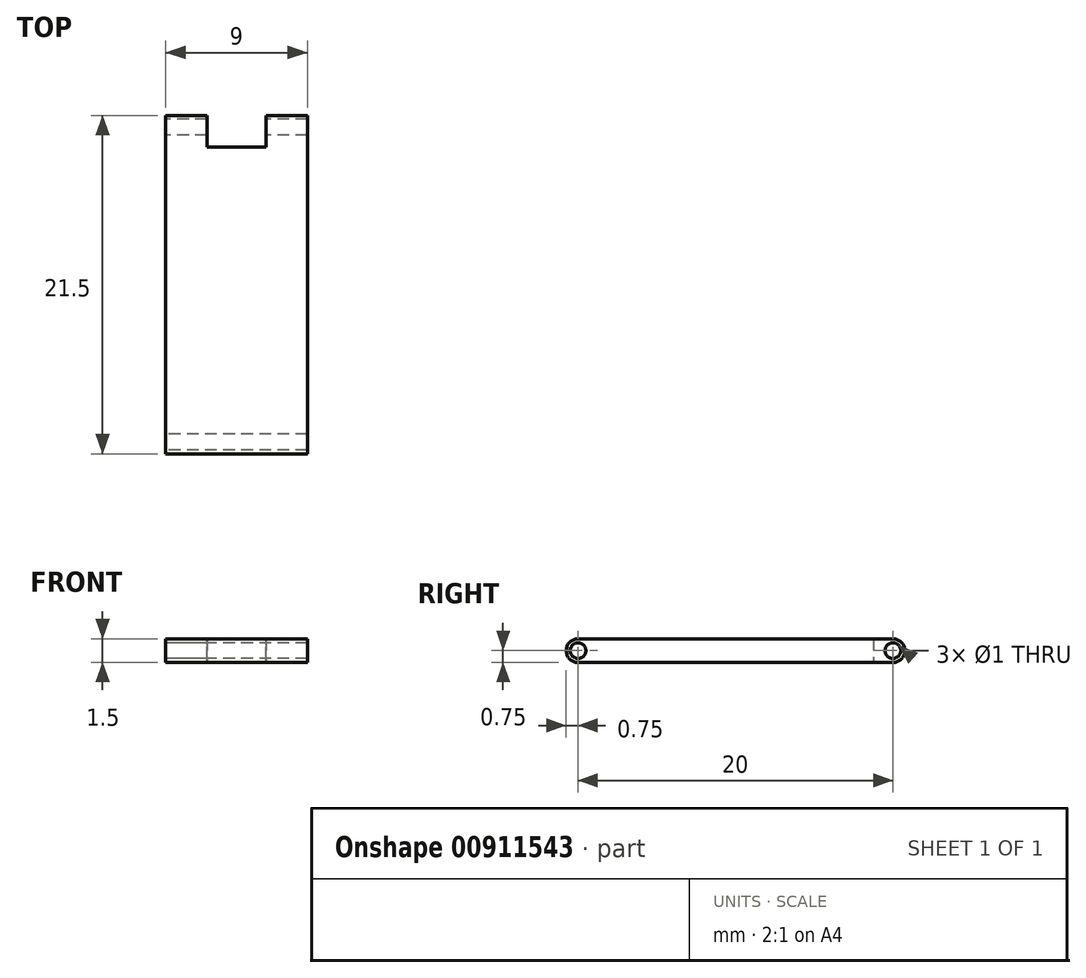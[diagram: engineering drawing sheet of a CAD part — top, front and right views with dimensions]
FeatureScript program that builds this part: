
annotation { "Feature Type Name" : "Feature", "Feature Type Description" : "" }
export const myFeature = defineFeature(function(context is Context, id is Id, definition is map)
    precondition{}
    {
        {
            var Q0;
            Q0=qCreatedBy(makeId("Right.planeOp"),FACE);
            var sketch = newSketch(context, id + "F0", { "sketchPlane" : qUnion([Q0])});
            skLineSegment(sketch, "E0.bottom", {"start": v(0, 0) * mm, "end": v(20, 0) * mm});
            skLineSegment(sketch, "E0.top", {"start": v(0, 1.5) * mm, "end": v(20, 1.5) * mm});
            skLineSegment(sketch, "E0.left", {"start": v(0, 0) * mm, "end": v(0, 1.5) * mm, "construction": true});
            skLineSegment(sketch, "E0.right", {"start": v(20, 0) * mm, "end": v(20, 1.5) * mm, "construction": true});
            skLineSegment(sketch, "E1", {"start": v(0, 0.75) * mm, "end": v(20, 0.75) * mm, "construction": true});
            skArc(sketch, "E2", {"start": v(0, 1.5) * mm, "mid": v(-0.75, 0.75) * mm, "end": v(0, 0) * mm});
            skArc(sketch, "E3", {"start": v(20, 0) * mm, "mid": v(20.75, 0.75) * mm, "end": v(20, 1.5) * mm});
            skCircle(sketch, "E4", {"center": v(0, 0.75) * mm, "radius": 0.5 * mm});
            skCircle(sketch, "E5", {"center": v(20, 0.75) * mm, "radius": 0.5 * mm});
            skSolve(sketch);
        }
        {
            var Q0;
            Q0 = qSketchRegion(id + "F0", true);
            extrude(context, id + "F1", {"entities" : qUnion([Q0]), "depth" : 9 * mm, "offsetDistance" : 25 * mm});
        }
        {
            var Q0;
            Q0=qCreatedBy(makeId("Top.planeOp"),FACE);
            var sketch = newSketch(context, id + "F2", { "sketchPlane" : qUnion([Q0])});
            skLineSegment(sketch, "E6", {"start": v(0, 20.75) * mm, "end": v(9, 20.75) * mm, "construction": true});
            skPoint(sketch, "E7.orphan", {"position": v(0, 20) * mm});
            skPoint(sketch, "E8.orphan", {"position": v(9, 20) * mm});
            skLineSegment(sketch, "E9.bottom", {"start": v(2.62, 20.75) * mm, "end": v(6.37, 20.75) * mm});
            skLineSegment(sketch, "E9.top", {"start": v(2.63, 18.75) * mm, "end": v(6.38, 18.75) * mm});
            skLineSegment(sketch, "E9.left", {"start": v(2.62, 20.75) * mm, "end": v(2.62, 18.75) * mm});
            skLineSegment(sketch, "E9.right", {"start": v(6.37, 20.75) * mm, "end": v(6.37, 18.75) * mm});
            skLineSegment(sketch, "E10", {"start": v(4.5, 20.75) * mm, "end": v(4.5, 16) * mm, "construction": true});
            skSolve(sketch);
        }
        {
            var Q0;
            Q0 = qSketchRegion(id + "F2", true);
            extrude(context, id + "F3", {"entities" : qUnion([Q0]), "operationType" : NewBodyOperationType.REMOVE, "endBound" : BoundingType.THROUGH_ALL, "depth" : 25 * mm, "offsetDistance" : 25 * mm});
        }
    });
